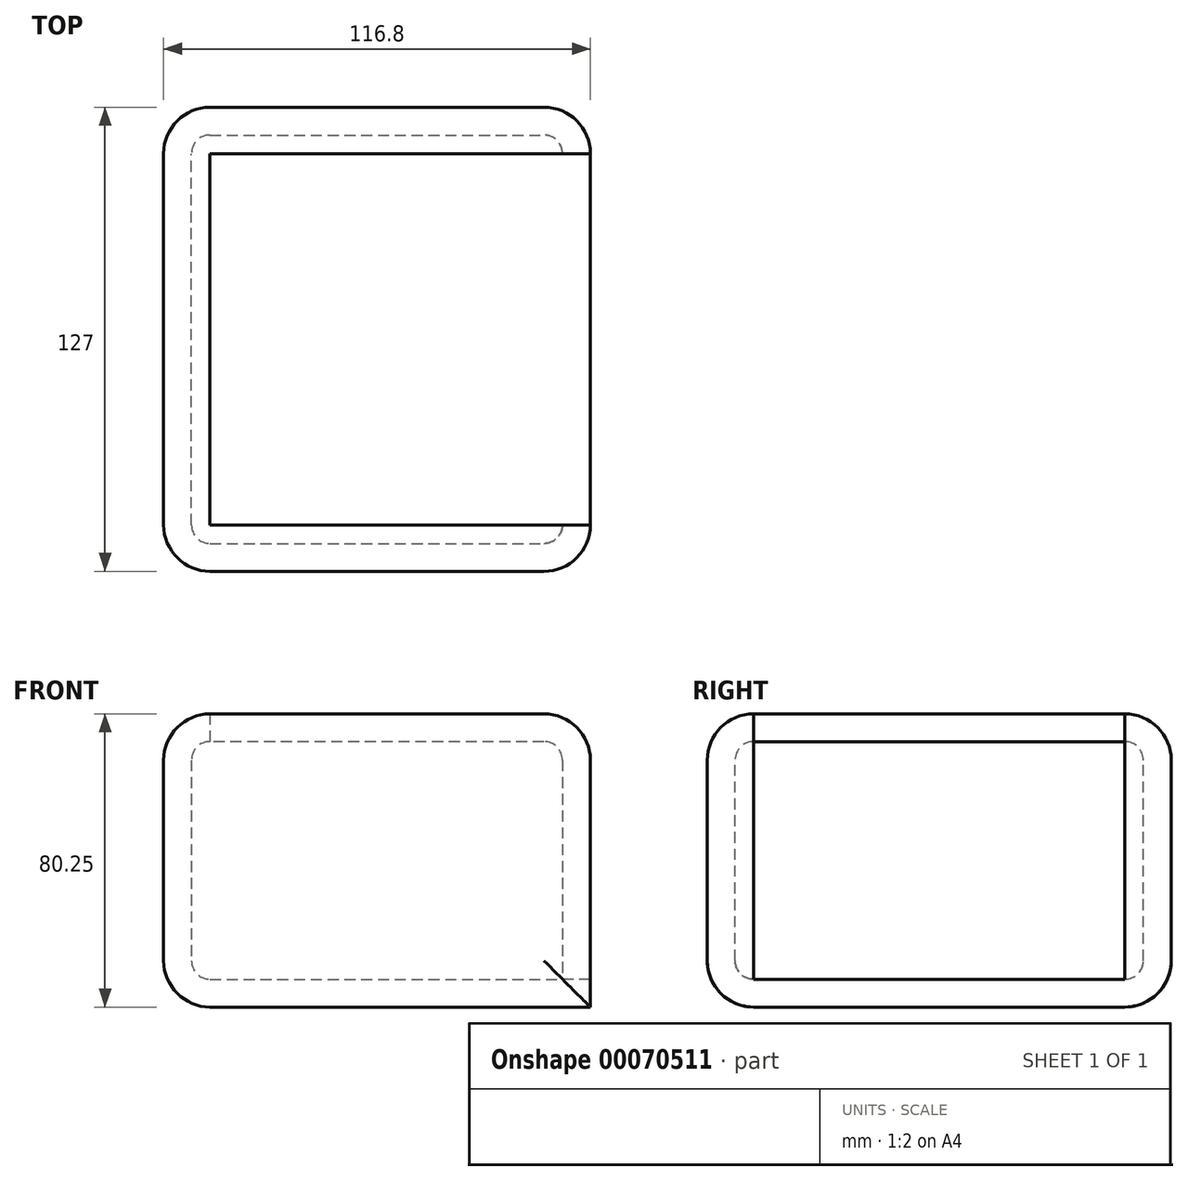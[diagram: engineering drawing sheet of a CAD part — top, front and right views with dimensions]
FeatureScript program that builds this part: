
annotation { "Feature Type Name" : "Feature", "Feature Type Description" : "" }
export const myFeature = defineFeature(function(context is Context, id is Id, definition is map)
    precondition{}
    {
        {
            var Q0;
            Q0=qCreatedBy(makeId("Front.planeOp"),FACE);
            var sketch = newSketch(context, id + "F0", { "sketchPlane" : qUnion([Q0])});
            skLineSegment(sketch, "E0.bottom", {"start": v(-57.06, 43.8) * mm, "end": v(59.74, 43.8) * mm});
            skLineSegment(sketch, "E0.top", {"start": v(-57.06, -36.46) * mm, "end": v(59.74, -36.46) * mm});
            skLineSegment(sketch, "E0.left", {"start": v(-57.06, 43.8) * mm, "end": v(-57.06, -36.46) * mm});
            skLineSegment(sketch, "E0.right", {"start": v(59.74, 43.8) * mm, "end": v(59.74, -36.46) * mm});
            skSolve(sketch);
        }
        {
            var Q0;
            Q0 = qSketchRegion(id + "F0", true);
            extrude(context, id + "F1", {"entities" : qUnion([Q0]), "endBound" : BoundingType.SYMMETRIC, "depth" : 127 * mm});
        }
        {
            var Q0;
            Q0=makeQuery(id+"F1.opExtrude","SWEPT_EDGE",EDGE,{"disambiguationData":[OSD([sQuery(id+"F0.wireOp",EDGE,"E0.bottom"),sQuery(id+"F0.wireOp",EDGE,"E0.left")])]});
            var Q1;
            Q1=makeQuery(id+"F1.opExtrude","CAP_EDGE",EDGE,{"disambiguationData":[OSD([sQuery(id+"F0.wireOp",EDGE,"E0.bottom")])],"isStart":true});
            var Q2;
            Q2=makeQuery(id+"F1.opExtrude","SWEPT_EDGE",EDGE,{"disambiguationData":[OSD([sQuery(id+"F0.wireOp",EDGE,"E0.bottom"),sQuery(id+"F0.wireOp",EDGE,"E0.right")])]});
            var Q3;
            Q3=makeQuery(id+"F1.opExtrude","CAP_EDGE",EDGE,{"disambiguationData":[OSD([sQuery(id+"F0.wireOp",EDGE,"E0.left")])],"isStart":false});
            var Q4;
            Q4=makeQuery(id+"F1.opExtrude","CAP_EDGE",EDGE,{"disambiguationData":[OSD([sQuery(id+"F0.wireOp",EDGE,"E0.left")])],"isStart":true});
            var Q5;
            Q5=makeQuery(id+"F1.opExtrude","CAP_EDGE",EDGE,{"disambiguationData":[OSD([sQuery(id+"F0.wireOp",EDGE,"E0.right")])],"isStart":false});
            var Q6;
            Q6=makeQuery(id+"F1.opExtrude","CAP_EDGE",EDGE,{"disambiguationData":[OSD([sQuery(id+"F0.wireOp",EDGE,"E0.right")])],"isStart":true});
            var Q7;
            Q7=makeQuery(id+"F1.opExtrude","CAP_EDGE",EDGE,{"disambiguationData":[OSD([sQuery(id+"F0.wireOp",EDGE,"E0.top")])],"isStart":true});
            var Q8;
            Q8=makeQuery(id+"F1.opExtrude","CAP_EDGE",EDGE,{"disambiguationData":[OSD([sQuery(id+"F0.wireOp",EDGE,"E0.top")])],"isStart":false});
            var Q9;
            Q9=makeQuery(id+"F1.opExtrude","SWEPT_EDGE",EDGE,{"disambiguationData":[OSD([sQuery(id+"F0.wireOp",EDGE,"E0.top"),sQuery(id+"F0.wireOp",EDGE,"E0.left")])]});
            var Q10;
            Q10=makeQuery(id+"F1.opExtrude","CAP_EDGE",EDGE,{"disambiguationData":[OSD([sQuery(id+"F0.wireOp",EDGE,"E0.bottom")])],"isStart":false});
            fillet(context, id + "F2", {"entities" : qUnion([Q0, Q1, Q2, Q3, Q4, Q5, Q6, Q7, Q8, Q9, Q10]), "radius" : 12.7 * mm, "tangentPropagation" : true, "allowEdgeOverflow" : false});
        }
        {
            var Q0;
            Q0=makeQuery(id+"F1.opExtrude","SWEPT_FACE",FACE,{"disambiguationData":[OSD([sQuery(id+"F0.wireOp",EDGE,"E0.bottom")])]});
            var Q1;
            Q1=makeQuery(id+"F1.opExtrude","SWEPT_FACE",FACE,{"disambiguationData":[OSD([sQuery(id+"F0.wireOp",EDGE,"E0.right")])]});
            var Q2;
            {var subQ0=sQuery(id+"F0.wireOp",EDGE,"E0.right");var subQ1=sQuery(id+"F0.wireOp",EDGE,"E0.bottom");Q2=makeQuery(id+"F2.opFillet","BLEND_FACE",FACE,{"disambiguationData":[OSD([subQ1,subQ0]),TDD([makeQuery(id+"F1.opExtrude","SWEPT_EDGE",EDGE,{"disambiguationData":[OSD([subQ1,subQ0])]})])]});}
            shell(context, id + "F3", {"entities" : qUnion([Q0, Q1, Q2]), "thickness" : 7.62 * mm});
        }
    });
